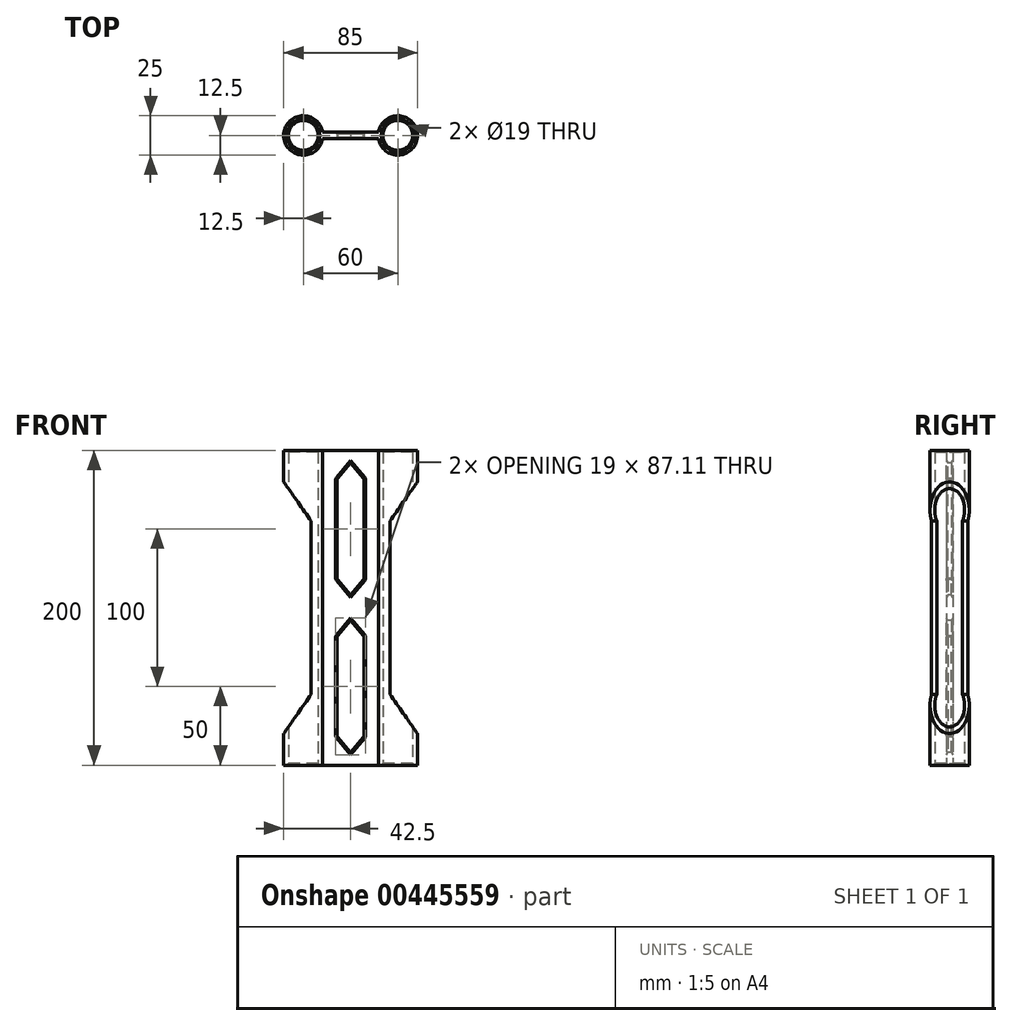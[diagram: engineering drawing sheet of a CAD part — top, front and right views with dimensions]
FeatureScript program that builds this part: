
annotation { "Feature Type Name" : "Feature", "Feature Type Description" : "" }
export const myFeature = defineFeature(function(context is Context, id is Id, definition is map)
    precondition{}
    {
        {
            var Q0;
            Q0=qCreatedBy(makeId("Top.planeOp"),FACE);
            var sketch = newSketch(context, id + "F0", { "sketchPlane" : qUnion([Q0])});
            skCircle(sketch, "E0", {"center": v(30, 0) * mm, "radius": 9.5 * mm});
            skCircle(sketch, "E1", {"center": v(30, 0) * mm, "radius": 12.5 * mm});
            skCircle(sketch, "E2.MirrorC", {"center": v(-30, 0) * mm, "radius": 12.5 * mm});
            skCircle(sketch, "E3.MirrorC", {"center": v(-30, 0) * mm, "radius": 9.5 * mm});
            skLineSegment(sketch, "E4.bottom", {"start": v(17.66, -2) * mm, "end": v(-17.66, -2) * mm});
            skLineSegment(sketch, "E4.top", {"start": v(17.66, 2) * mm, "end": v(-17.66, 2) * mm});
            skLineSegment(sketch, "E4.left", {"start": v(17.66, -2) * mm, "end": v(17.66, 2) * mm});
            skLineSegment(sketch, "E4.right", {"start": v(-17.66, -2) * mm, "end": v(-17.66, 2) * mm});
            skPoint(sketch, "E4.middle", {"position": v(0, 0) * mm});
            skSolve(sketch);
        }
        {
            var Q0;
            Q0 = qSketchRegion(id + "F0", true);
            extrude(context, id + "F1", {"entities" : qUnion([Q0]), "depth" : 200 * mm, "symmetric" : true});
        }
        {
            var Q0;
            Q0=qCreatedBy(makeId("Front.planeOp"),FACE);
            var sketch = newSketch(context, id + "F2", { "sketchPlane" : qUnion([Q0])});
            skLineSegment(sketch, "E5", {"start": v(0, 0) * mm, "end": v(42.5, 0) * mm});
            skLineSegment(sketch, "E6", {"start": v(42.5, 0) * mm, "end": v(42.5, 80) * mm});
            skLineSegment(sketch, "E7", {"start": v(42.5, 80) * mm, "end": v(25, 55) * mm});
            skLineSegment(sketch, "E8", {"start": v(25, 55) * mm, "end": v(25, 0) * mm});
            skLineSegment(sketch, "E9.MirrorCS", {"start": v(-42.5, 80) * mm, "end": v(-25, 55) * mm});
            skLineSegment(sketch, "E10.MirrorCS", {"start": v(-42.5, 0) * mm, "end": v(-42.5, 80) * mm});
            skLineSegment(sketch, "E11.MirrorCS", {"start": v(-25, 55) * mm, "end": v(-25, 0) * mm});
            skLineSegment(sketch, "E12.MirrorCS", {"start": v(0, 0) * mm, "end": v(-42.5, 0) * mm});
            skLineSegment(sketch, "E13.MirrorCS", {"start": v(42.5, 0) * mm, "end": v(42.5, -80) * mm});
            skLineSegment(sketch, "E14.MirrorCS", {"start": v(42.5, -80) * mm, "end": v(25, -55) * mm});
            skLineSegment(sketch, "E15.MirrorCS", {"start": v(25, -55) * mm, "end": v(25, 0) * mm});
            skLineSegment(sketch, "E16.MirrorCS", {"start": v(-25, -55) * mm, "end": v(-25, 0) * mm});
            skLineSegment(sketch, "E17.MirrorCS", {"start": v(-42.5, -80) * mm, "end": v(-25, -55) * mm});
            skLineSegment(sketch, "E18.MirrorCS", {"start": v(-42.5, 0) * mm, "end": v(-42.5, -80) * mm});
            skLineSegment(sketch, "E19", {"start": v(0, 0) * mm, "end": v(0, 8) * mm});
            skLineSegment(sketch, "E20", {"start": v(0, 8) * mm, "end": v(8.5, 18.13) * mm});
            skLineSegment(sketch, "E21", {"start": v(8.5, 18.13) * mm, "end": v(8.5, 81.87) * mm});
            skLineSegment(sketch, "E22", {"start": v(8.5, 81.87) * mm, "end": v(0, 92) * mm});
            skLineSegment(sketch, "E23.MirrorCS", {"start": v(-8.5, 81.87) * mm, "end": v(0, 92) * mm});
            skLineSegment(sketch, "E24.MirrorCS", {"start": v(-8.5, 18.13) * mm, "end": v(-8.5, 81.87) * mm});
            skLineSegment(sketch, "E25.MirrorCS", {"start": v(0, 8) * mm, "end": v(-8.5, 18.13) * mm});
            skLineSegment(sketch, "E26.MirrorCS", {"start": v(-8.5, -81.87) * mm, "end": v(0, -92) * mm});
            skLineSegment(sketch, "E27.MirrorCS", {"start": v(8.5, -81.87) * mm, "end": v(0, -92) * mm});
            skLineSegment(sketch, "E28.MirrorCS", {"start": v(-8.5, -18.13) * mm, "end": v(-8.5, -81.87) * mm});
            skLineSegment(sketch, "E29.MirrorCS", {"start": v(8.5, -18.13) * mm, "end": v(8.5, -81.87) * mm});
            skLineSegment(sketch, "E30.MirrorCS", {"start": v(0, -8) * mm, "end": v(-8.5, -18.13) * mm});
            skLineSegment(sketch, "E31.MirrorCS", {"start": v(0, -8) * mm, "end": v(8.5, -18.13) * mm});
            skSolve(sketch);
        }
        {
            var Q0;
            Q0 = qSketchRegion(id + "F2", true);
            extrude(context, id + "F3", {"entities" : qUnion([Q0]), "operationType" : NewBodyOperationType.REMOVE, "oppositeDirection" : true, "depth" : 100 * mm, "symmetric" : true});
        }
        {
            var Q0;
            Q0=makeQuery(id+"F1.opExtrude","CAP_EDGE",EDGE,{"disambiguationData":[OSD([sQuery(id+"F0.wireOp",EDGE,"E3.MirrorC")])],"isStart":true});
            var Q1;
            Q1=makeQuery(id+"F1.opExtrude","CAP_EDGE",EDGE,{"disambiguationData":[OSD([sQuery(id+"F0.wireOp",EDGE,"E0")])],"isStart":true});
            var Q2;
            Q2=makeQuery(id+"F1.opExtrude","CAP_EDGE",EDGE,{"disambiguationData":[OSD([sQuery(id+"F0.wireOp",EDGE,"E0")])],"isStart":false});
            var Q3;
            Q3=makeQuery(id+"F1.opExtrude","CAP_EDGE",EDGE,{"disambiguationData":[OSD([sQuery(id+"F0.wireOp",EDGE,"E3.MirrorC")])],"isStart":false});
            var Q4;
            Q4=makeQuery(id+"F3.boolean.opBoolean","COPY",FACE,{"derivedFrom":makeQuery(id+"F3.opExtrude","SWEPT_FACE",FACE,{"disambiguationData":[OSD([sQuery(id+"F2.wireOp",EDGE,"E24.MirrorCS")])]})});
            var Q5;
            Q5=makeQuery(id+"F3.boolean.opBoolean","COPY",FACE,{"derivedFrom":makeQuery(id+"F3.opExtrude","SWEPT_FACE",FACE,{"disambiguationData":[OSD([sQuery(id+"F2.wireOp",EDGE,"E21")])]})});
            var Q6;
            Q6=makeQuery(id+"F3.boolean.opBoolean","COPY",FACE,{"derivedFrom":makeQuery(id+"F3.opExtrude","SWEPT_FACE",FACE,{"disambiguationData":[OSD([sQuery(id+"F2.wireOp",EDGE,"E28.MirrorCS")])]})});
            var Q7;
            Q7=makeQuery(id+"F3.boolean.opBoolean","COPY",FACE,{"derivedFrom":makeQuery(id+"F3.opExtrude","SWEPT_FACE",FACE,{"disambiguationData":[OSD([sQuery(id+"F2.wireOp",EDGE,"E29.MirrorCS")])]})});
            chamfer(context, id + "F4", {"entities" : qUnion([Q0, Q1, Q2, Q3, Q4, Q5, Q6, Q7]), "width" : 1 * mm, "tangentPropagation" : true});
        }
    });
